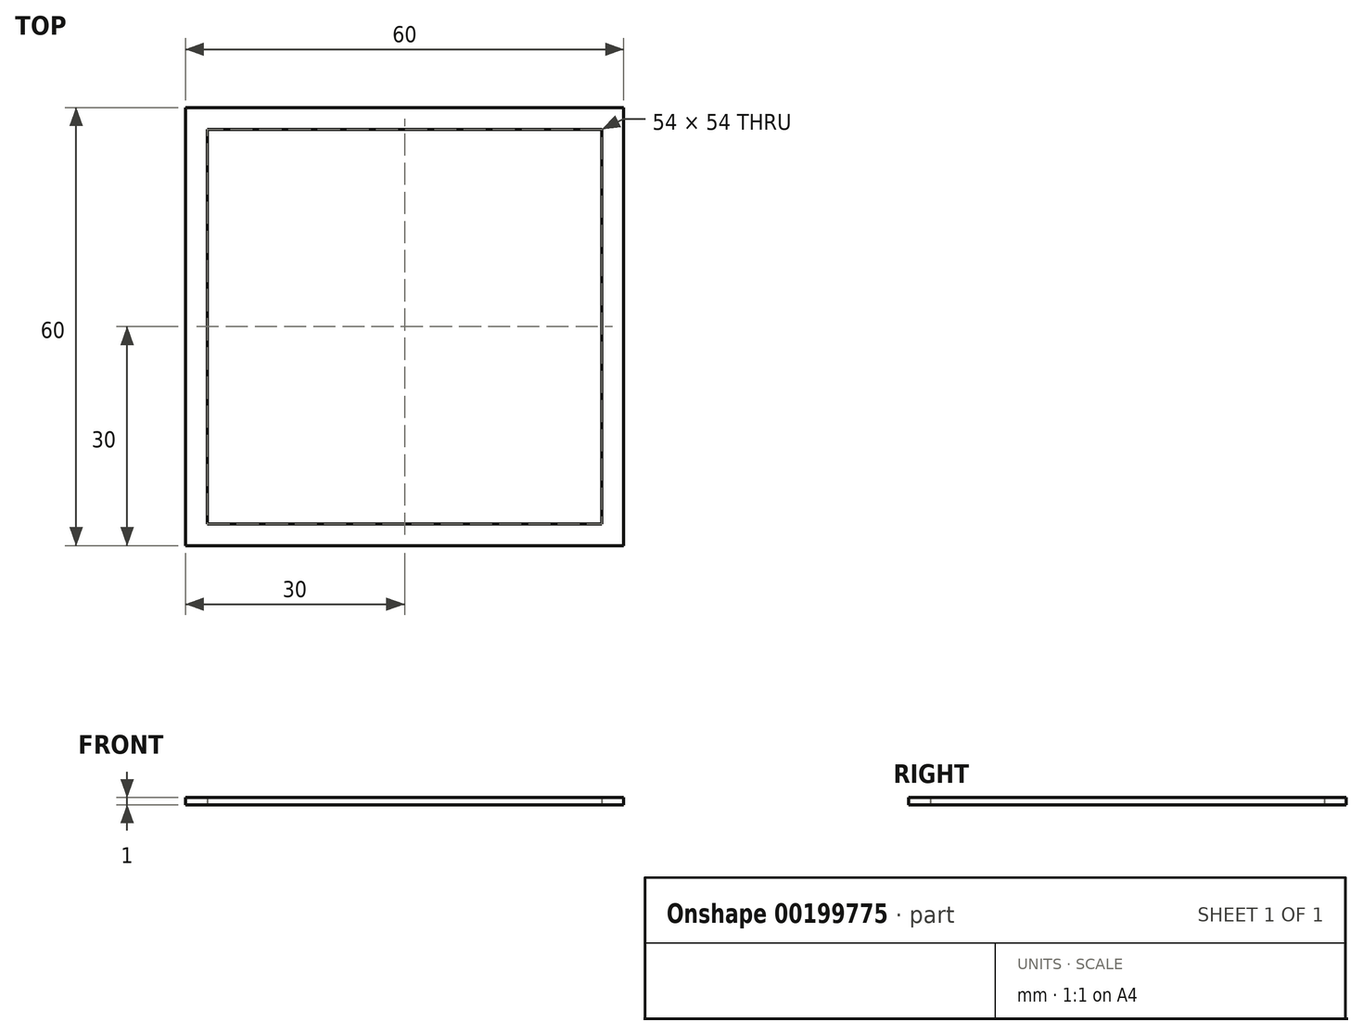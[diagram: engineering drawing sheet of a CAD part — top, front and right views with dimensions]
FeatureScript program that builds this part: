
annotation { "Feature Type Name" : "Feature", "Feature Type Description" : "" }
export const myFeature = defineFeature(function(context is Context, id is Id, definition is map)
    precondition{}
    {
        {
            var Q0;
            Q0=qCreatedBy(makeId("Top.planeOp"),FACE);
            var sketch = newSketch(context, id + "F0", { "sketchPlane" : qUnion([Q0])});
            skLineSegment(sketch, "E0.bottom", {"start": v(30, 30) * mm, "end": v(-30, 30) * mm});
            skLineSegment(sketch, "E0.top", {"start": v(30, -30) * mm, "end": v(-30, -30) * mm});
            skLineSegment(sketch, "E0.left", {"start": v(30, 30) * mm, "end": v(30, -30) * mm});
            skLineSegment(sketch, "E0.right", {"start": v(-30, 30) * mm, "end": v(-30, -30) * mm});
            skPoint(sketch, "E0.middle", {"position": v(0, 0) * mm});
            skLineSegment(sketch, "E1.0", {"start": v(27, 27) * mm, "end": v(-27, 27) * mm});
            skLineSegment(sketch, "E1.1", {"start": v(27, 27) * mm, "end": v(27, -27) * mm});
            skLineSegment(sketch, "E1.2", {"start": v(27, -27) * mm, "end": v(-27, -27) * mm});
            skLineSegment(sketch, "E1.3", {"start": v(-27, 27) * mm, "end": v(-27, -27) * mm});
            skSolve(sketch);
        }
        {
            var Q0;
            Q0 = qSketchRegion(id + "F0", true);
            extrude(context, id + "F1", {"entities" : qUnion([Q0]), "depth" : 1 * mm});
        }
    });
